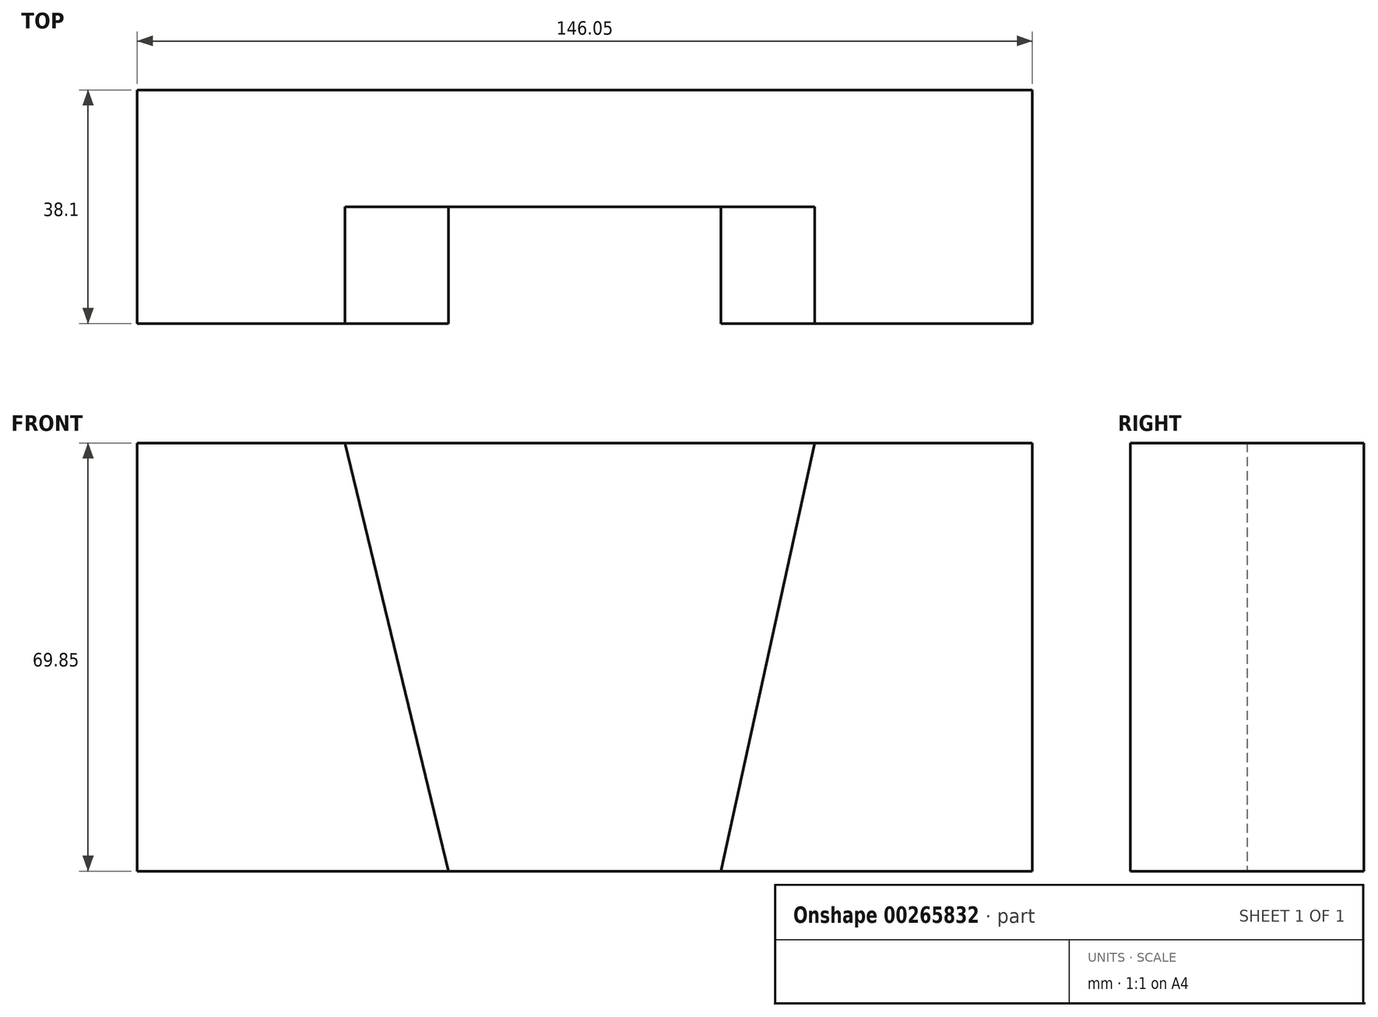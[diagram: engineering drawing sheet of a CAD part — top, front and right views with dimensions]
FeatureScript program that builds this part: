
annotation { "Feature Type Name" : "Feature", "Feature Type Description" : "" }
export const myFeature = defineFeature(function(context is Context, id is Id, definition is map)
    precondition{}
    {
        {
            var Q0;
            Q0=qCreatedBy(makeId("Front.planeOp"),FACE);
            var sketch = newSketch(context, id + "F0", { "sketchPlane" : qUnion([Q0])});
            skLineSegment(sketch, "E0", {"start": v(-79.58, -52.9) * mm, "end": v(66.47, -52.9) * mm});
            skLineSegment(sketch, "E1", {"start": v(-79.58, -52.9) * mm, "end": v(-79.58, 16.95) * mm});
            skLineSegment(sketch, "E2", {"start": v(-79.58, 16.95) * mm, "end": v(66.47, 16.95) * mm});
            skLineSegment(sketch, "E3", {"start": v(66.47, 16.95) * mm, "end": v(66.47, -52.9) * mm});
            skSolve(sketch);
        }
        {
            var Q0;
            Q0=makeQuery(id+"F0.imprint","IMPRINT",FACE,{"disambiguationData":[TD([[makeQuery(id+"F0.imprint","IMPRINT",EDGE,{"derivedFrom":sQuery(id+"F0.wireOp",EDGE,"E0")}),1.0]])]});
            extrude(context, id + "F1", {"entities" : qUnion([Q0]), "depth" : 38.1 * mm});
        }
        {
            var Q0;
            Q0=makeQuery(id+"F1.opExtrude","CAP_FACE",FACE,{"disambiguationData":[OSD([sQuery(id+"F0.wireOp",EDGE,"E0"),sQuery(id+"F0.wireOp",EDGE,"E1"),sQuery(id+"F0.wireOp",EDGE,"E2"),sQuery(id+"F0.wireOp",EDGE,"E3")])],"isStart":false});
            var sketch = newSketch(context, id + "F2", { "sketchPlane" : qUnion([Q0])});
            skLineSegment(sketch, "E4", {"start": v(66.47, -52.9) * mm, "end": v(15.67, -52.9) * mm});
            skLineSegment(sketch, "E5", {"start": v(15.67, -52.9) * mm, "end": v(66.47, -52.9) * mm});
            skLineSegment(sketch, "E6", {"start": v(-79.58, -52.9) * mm, "end": v(-28.78, -52.9) * mm});
            skLineSegment(sketch, "E7", {"start": v(-28.78, -52.9) * mm, "end": v(-79.58, -52.9) * mm});
            skLineSegment(sketch, "E8", {"start": v(-45.7, 16.95) * mm, "end": v(-28.78, -52.9) * mm});
            skLineSegment(sketch, "E9", {"start": v(30.95, 16.95) * mm, "end": v(15.67, -52.9) * mm});
            skSolve(sketch);
        }
        {
            var Q0;
            Q0 = qSketchRegion(id + "F2", true);
            var Q1;
            {var subQ0=sQuery(id+"F2.wireOp",EDGE,"E8");Q1=makeQuery(id+"F2.imprint","IMPRINT",FACE,{"disambiguationData":[TD([[makeQuery(id+"F2.imprint","IMPRINT",EDGE,{"derivedFrom":subQ0}),1.0]])]});}
            extrude(context, id + "F3", {"entities" : qUnion([Q0, Q1]), "operationType" : NewBodyOperationType.REMOVE, "oppositeDirection" : true, "depth" : 19.05 * mm});
        }
    });
